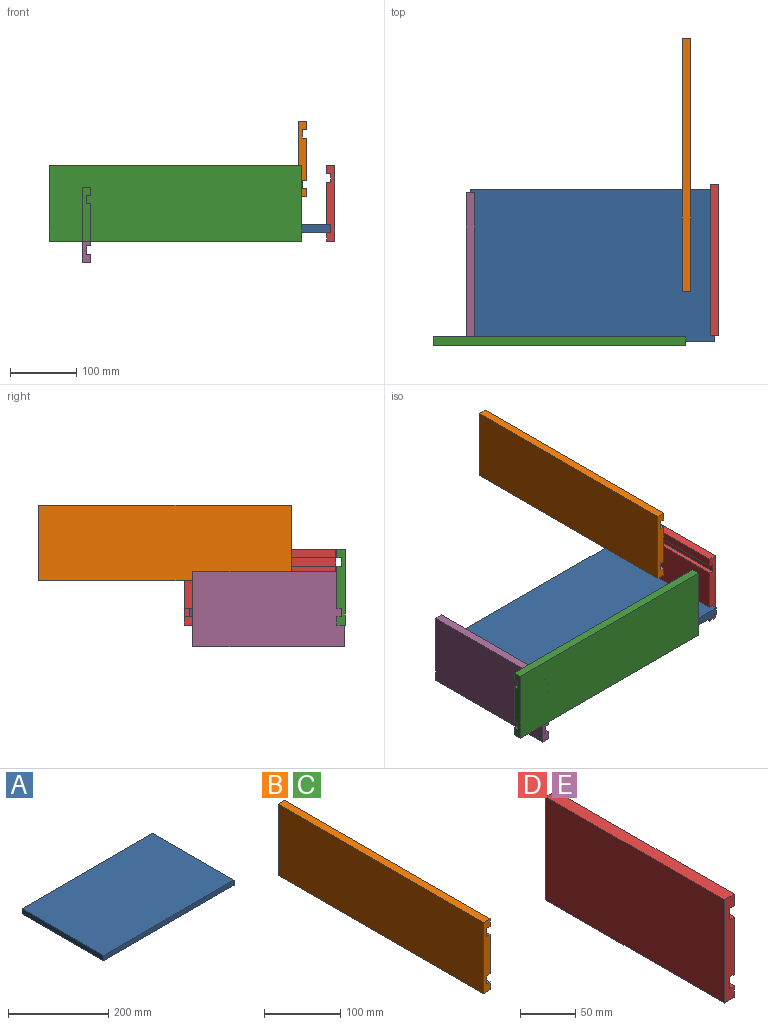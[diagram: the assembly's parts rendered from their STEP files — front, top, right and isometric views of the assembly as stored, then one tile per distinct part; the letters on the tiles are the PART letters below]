
ASSEMBLY  parts=5 mates=5
PART A: 6 faces, bbox 368.3x228.6x12.7 mm
  f0: plane 228.6x12.7mm, normal (-1,0,0), area 2903.2mm2, adj f1,f3,f4,f5
  f1: plane 368.3x12.7mm, normal (0,-1,0), area 4677.4mm2, adj f0,f2,f4,f5
  f2: plane 228.6x12.7mm, normal (1,0,0), area 2903.2mm2, adj f1,f3,f4,f5
  f3: plane 368.3x12.7mm, normal (0,1,0), area 4677.4mm2, adj f0,f2,f4,f5
  f4: plane 368.3x228.6mm, normal (0,0,1), area 84193.4mm2, adj f0,f1,f2,f3
  f5: plane 368.3x228.6mm, normal (0,0,-1), area 84193.4mm2, adj f0,f1,f2,f3
PART B: 14 faces, bbox 12.7x381x114.3 mm
  f0: plane 381x12.7mm, normal (1,0,0), area 4838.7mm2, adj f1,f11,f12,f13
  f1: plane 381x6.35mm, normal (0,0,-1), area 2419.3mm2, adj f0,f2,f12,f13
  f2: plane 381x63.5mm, normal (1,0,0), area 24193.5mm2, adj f1,f3,f12,f13
  f3: plane 381x6.35mm, normal (0,0,1), area 2419.3mm2, adj f2,f4,f12,f13
  f4: plane 381x12.7mm, normal (1,0,0), area 4838.7mm2, adj f3,f5,f12,f13
  f5: plane 381x6.35mm, normal (0,0,-1), area 2419.3mm2, adj f4,f6,f12,f13
  f6: plane 381x12.7mm, normal (1,0,0), area 4838.7mm2, adj f5,f7,f12,f13
  f7: plane 381x12.7mm, normal (0,0,1), area 4838.7mm2, adj f6,f8,f12,f13
  f8: plane 381x114.3mm, normal (-1,0,0), area 43548.3mm2, adj f7,f9,f12,f13
  f9: plane 381x12.7mm, normal (0,0,-1), area 4838.7mm2, adj f8,f10,f12,f13
  f10: plane 381x12.7mm, normal (1,0,0), area 4838.7mm2, adj f9,f11,f12,f13
  f11: plane 381x6.35mm, normal (0,0,1), area 2419.3mm2, adj f0,f10,f12,f13
  f12: plane 114.3x12.7mm, normal (0,-1,0), area 1290.3mm2, adj f0,f1,f2,f3,f4,f5,f6,f7
  f13: plane 114.3x12.7mm, normal (0,1,0), area 1290.3mm2, adj f0,f1,f2,f3,f4,f5,f6,f7
PART C: same geometry as B
PART D: 14 faces, bbox 12.7x228.6x114.3 mm
  f0: plane 228.6x12.7mm, normal (1,0,0), area 2903.2mm2, adj f1,f11,f12,f13
  f1: plane 228.6x6.35mm, normal (0,0,-1), area 1451.6mm2, adj f0,f2,f12,f13
  f2: plane 228.6x63.5mm, normal (1,0,0), area 14516.1mm2, adj f1,f3,f12,f13
  f3: plane 228.6x6.35mm, normal (0,0,1), area 1451.6mm2, adj f2,f4,f12,f13
  f4: plane 228.6x12.7mm, normal (1,0,0), area 2903.2mm2, adj f3,f5,f12,f13
  f5: plane 228.6x6.35mm, normal (0,0,-1), area 1451.6mm2, adj f4,f6,f12,f13
  f6: plane 228.6x12.7mm, normal (1,0,0), area 2903.2mm2, adj f5,f7,f12,f13
  f7: plane 228.6x12.7mm, normal (0,0,1), area 2903.2mm2, adj f6,f8,f12,f13
  f8: plane 228.6x114.3mm, normal (-1,0,0), area 26129mm2, adj f7,f9,f12,f13
  f9: plane 228.6x12.7mm, normal (0,0,-1), area 2903.2mm2, adj f8,f10,f12,f13
  f10: plane 228.6x12.7mm, normal (1,0,0), area 2903.2mm2, adj f9,f11,f12,f13
  f11: plane 228.6x6.35mm, normal (0,0,1), area 1451.6mm2, adj f0,f10,f12,f13
  f12: plane 114.3x12.7mm, normal (0,-1,0), area 1290.3mm2, adj f0,f1,f2,f3,f4,f5,f6,f7
  f13: plane 114.3x12.7mm, normal (0,1,0), area 1290.3mm2, adj f0,f1,f2,f3,f4,f5,f6,f7
PART E: same geometry as D
PLACE A t=(8.04,2.12,-10.14)mm fixed
PLACE B t=(143.05,343.99,43.69)mm
PLACE C rot(axis=(0,0,1),90deg) t=(-232.57,-118.53,-22.84)mm
PLACE D rot(axis=(0,1,0),180deg) t=(198.54,124.34,91.46)mm
PLACE E t=(-182.46,111.43,-55.54)mm
MATE planar C.f1 <-> A.f4  axis (0,0,-1) through (-42.07,-109.01,2.56)mm
MATE planar E.f0 <-> A.f0  axis (1,0,0) through (-176.11,-2.87,-36.49)mm
MATE planar A.f1 <-> C.f0  axis (0,-1,0) through (8.04,-112.18,-3.79)mm
MATE planar C.f7 <-> D.f9  axis (0,0,1) through (-42.07,-112.18,91.46)mm
MATE planar D.f0 <-> A.f2  axis (-1,0,0) through (192.19,10.04,72.41)mm
